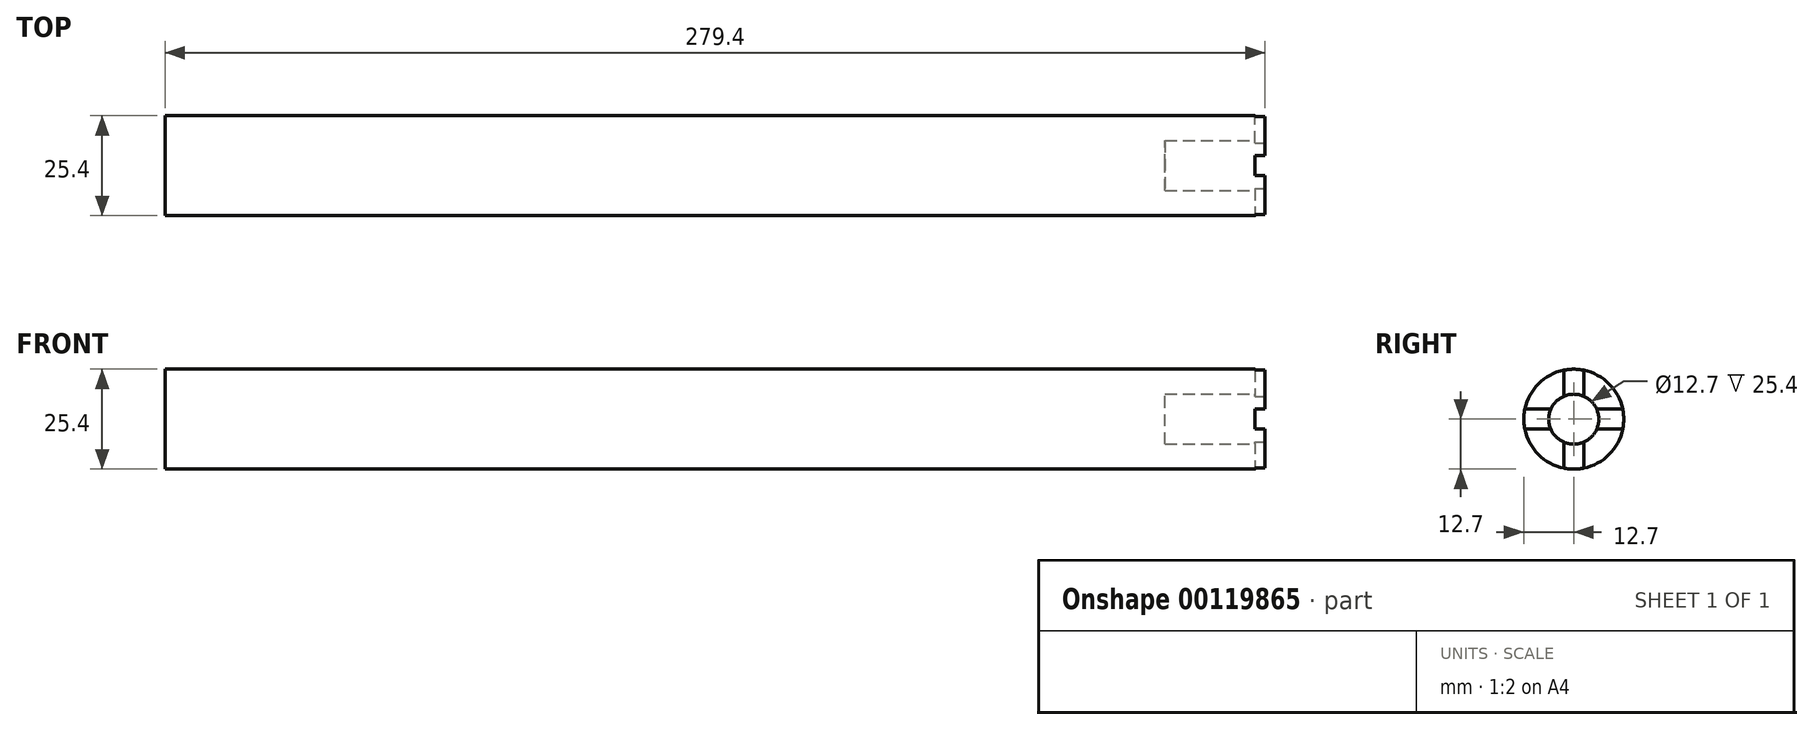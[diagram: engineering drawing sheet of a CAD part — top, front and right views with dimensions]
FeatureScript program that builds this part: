
annotation { "Feature Type Name" : "Feature", "Feature Type Description" : "" }
export const myFeature = defineFeature(function(context is Context, id is Id, definition is map)
    precondition{}
    {
        {
            var Q0;
            Q0=qCreatedBy(makeId("Right.planeOp"),FACE);
            var sketch = newSketch(context, id + "F0", { "sketchPlane" : qUnion([Q0])});
            skCircle(sketch, "E0", {"center": v(0, 0) * mm, "radius": 12.7 * mm});
            skSolve(sketch);
        }
        {
            var Q0;
            Q0 = qSketchRegion(id + "F0", true);
            extrude(context, id + "F1", {"entities" : qUnion([Q0]), "oppositeDirection" : true, "depth" : 279.4 * mm});
        }
        {
            var Q0;
            Q0=makeQuery(id+"F1.opExtrude","CAP_FACE",FACE,{"disambiguationData":[OSD([sQuery(id+"F0.wireOp",EDGE,"E0")])],"isStart":true});
            var sketch = newSketch(context, id + "F2", { "sketchPlane" : qUnion([Q0])});
            skCircle(sketch, "E1", {"center": v(0, 0) * mm, "radius": 6.35 * mm});
            skSolve(sketch);
        }
        {
            var Q0;
            Q0 = qSketchRegion(id + "F2", true);
            extrude(context, id + "F3", {"entities" : qUnion([Q0]), "operationType" : NewBodyOperationType.REMOVE, "oppositeDirection" : true, "depth" : 25.4 * mm});
        }
        {
            var Q0;
            Q0=qCreatedBy(makeId("Right.planeOp"),FACE);
            var sketch = newSketch(context, id + "F4", { "sketchPlane" : qUnion([Q0])});
            skLineSegment(sketch, "E2", {"start": v(0, 27.15) * mm, "end": v(0, -32.77) * mm, "construction": true});
            skLineSegment(sketch, "E3", {"start": v(-30.49, 0) * mm, "end": v(37.07, 0) * mm, "construction": true});
            skLineSegment(sketch, "E4.bottom", {"start": v(-2.54, 21.55) * mm, "end": v(2.54, 21.55) * mm});
            skLineSegment(sketch, "E4.top", {"start": v(-2.54, 4.62) * mm, "end": v(2.54, 4.62) * mm});
            skLineSegment(sketch, "E4.left", {"start": v(-2.54, 21.55) * mm, "end": v(-2.54, 4.62) * mm});
            skLineSegment(sketch, "E4.right", {"start": v(2.54, 21.55) * mm, "end": v(2.54, 4.62) * mm});
            skLineSegment(sketch, "E5.bottom", {"start": v(4.55, 2.54) * mm, "end": v(21.48, 2.54) * mm});
            skLineSegment(sketch, "E5.top", {"start": v(4.55, -2.54) * mm, "end": v(21.48, -2.54) * mm});
            skLineSegment(sketch, "E5.left", {"start": v(4.55, 2.54) * mm, "end": v(4.55, -2.54) * mm});
            skLineSegment(sketch, "E5.right", {"start": v(21.48, 2.54) * mm, "end": v(21.48, -2.54) * mm});
            skLineSegment(sketch, "E6.bottom", {"start": v(-2.54, -3.44) * mm, "end": v(2.54, -3.44) * mm});
            skLineSegment(sketch, "E6.top", {"start": v(-2.54, -20.37) * mm, "end": v(2.54, -20.37) * mm});
            skLineSegment(sketch, "E6.left", {"start": v(-2.54, -3.44) * mm, "end": v(-2.54, -20.37) * mm});
            skLineSegment(sketch, "E6.right", {"start": v(2.54, -3.44) * mm, "end": v(2.54, -20.37) * mm});
            skLineSegment(sketch, "E7.bottom", {"start": v(-3.97, 2.54) * mm, "end": v(-20.9, 2.54) * mm});
            skLineSegment(sketch, "E7.top", {"start": v(-3.97, -2.54) * mm, "end": v(-20.9, -2.54) * mm});
            skLineSegment(sketch, "E7.left", {"start": v(-3.97, 2.54) * mm, "end": v(-3.97, -2.54) * mm});
            skLineSegment(sketch, "E7.right", {"start": v(-20.9, 2.54) * mm, "end": v(-20.9, -2.54) * mm});
            skSolve(sketch);
        }
        {
            var Q0;
            Q0 = qSketchRegion(id + "F4", true);
            extrude(context, id + "F5", {"entities" : qUnion([Q0]), "operationType" : NewBodyOperationType.REMOVE, "oppositeDirection" : true, "depth" : 2.54 * mm});
        }
    });
